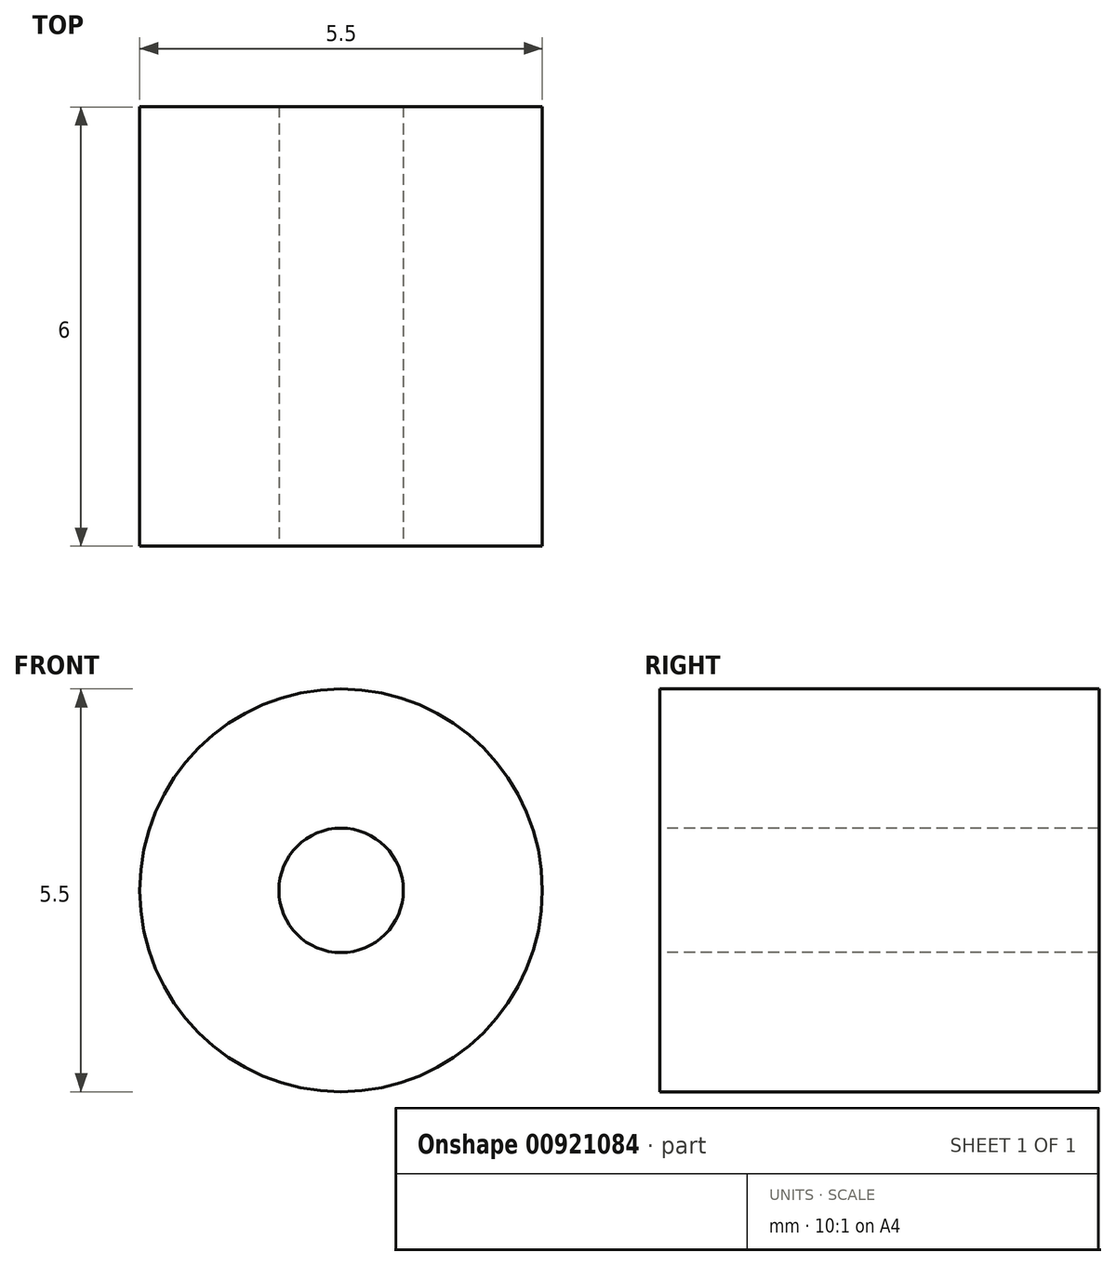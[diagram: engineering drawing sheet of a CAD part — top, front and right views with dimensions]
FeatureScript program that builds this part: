
annotation { "Feature Type Name" : "Feature", "Feature Type Description" : "" }
export const myFeature = defineFeature(function(context is Context, id is Id, definition is map)
    precondition{}
    {
        {
            var Q0;
            Q0=qCreatedBy(makeId("Right.planeOp"),FACE);
            var sketch = newSketch(context, id + "F0", { "sketchPlane" : qUnion([Q0])});
            skLineSegment(sketch, "E0", {"start": v(-11.64, 0) * mm, "end": v(12.3, 0) * mm, "construction": true});
            skLineSegment(sketch, "E1", {"start": v(-0.84, 2.75) * mm, "end": v(5.16, 2.75) * mm});
            skLineSegment(sketch, "E2", {"start": v(5.16, 0.85) * mm, "end": v(-0.84, 0.85) * mm});
            skLineSegment(sketch, "E3", {"start": v(-0.84, 2.75) * mm, "end": v(-0.84, 0.85) * mm});
            skLineSegment(sketch, "E4", {"start": v(5.16, 2.75) * mm, "end": v(5.16, 0.85) * mm});
            skSolve(sketch);
        }
        {
            var Q0;
            Q0 = qSketchRegion(id + "F0", true);
            var Q1;
            Q1=sQuery(id+"F0.wireOp",EDGE,"E0");
            revolve(context, id + "F1", {"surfaceOperationType" : NewSurfaceOperationType.NEW, "entities" : qUnion([Q0]), "axis" : qUnion([Q1]), "revolveType" : RevolveType.FULL});
        }
    });
